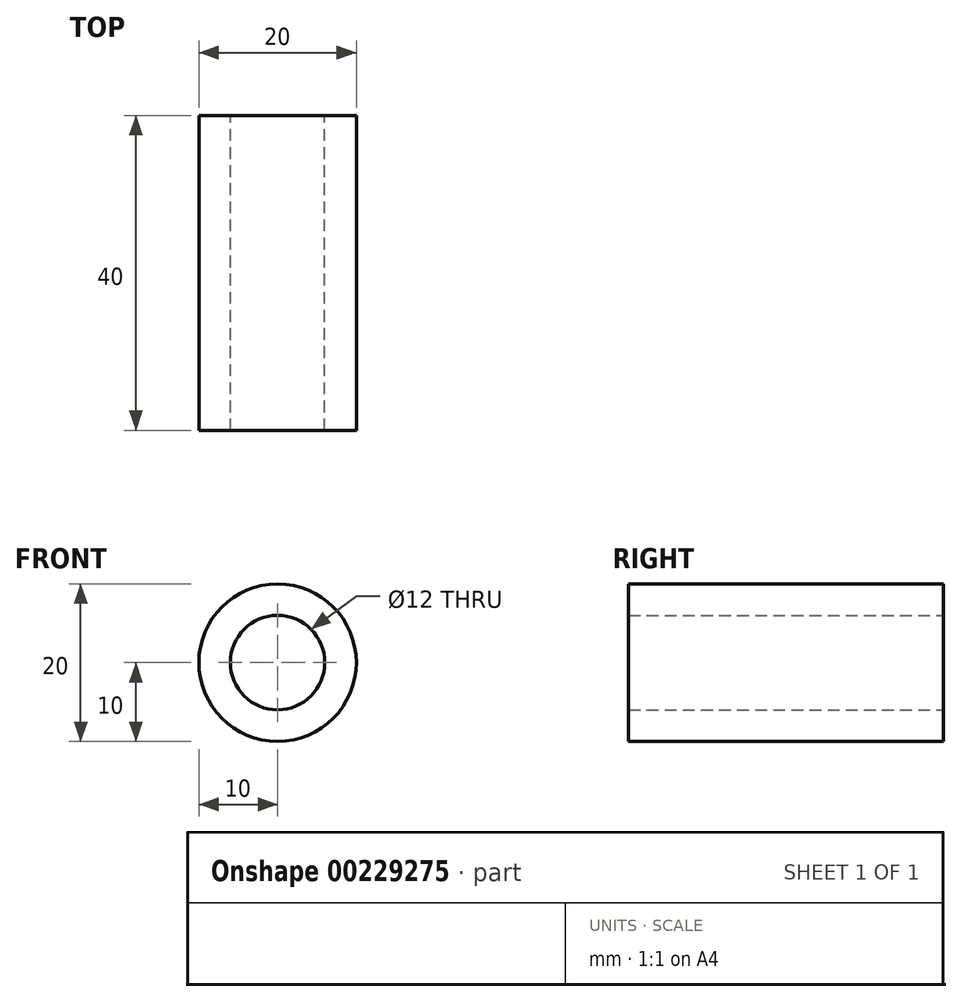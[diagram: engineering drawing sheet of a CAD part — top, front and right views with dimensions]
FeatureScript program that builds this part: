
annotation { "Feature Type Name" : "Feature", "Feature Type Description" : "" }
export const myFeature = defineFeature(function(context is Context, id is Id, definition is map)
    precondition{}
    {
        {
            var Q0;
            Q0=qCreatedBy(makeId("Front.planeOp"),FACE);
            var sketch = newSketch(context, id + "F0", { "sketchPlane" : qUnion([Q0])});
            skCircle(sketch, "E0", {"center": v(0, 0) * mm, "radius": 10 * mm});
            skCircle(sketch, "E1", {"center": v(0, 0) * mm, "radius": 6 * mm});
            skSolve(sketch);
        }
        {
            var Q0;
            Q0=qSketchRegion(id+"F0",true);
            var Q1;
            Q1=makeQuery(id+"F0.imprint","IMPRINT",FACE,{"disambiguationData":[TD([[makeQuery(id+"F0.imprint","IMPRINT",EDGE,{"derivedFrom":sQuery(id+"F0.wireOp",EDGE,"E0")}),1.0]])]});
            extrude(context, id + "F1", {"entities" : qUnion([Q0, Q1]), "depth" : 40 * mm});
        }
    });
